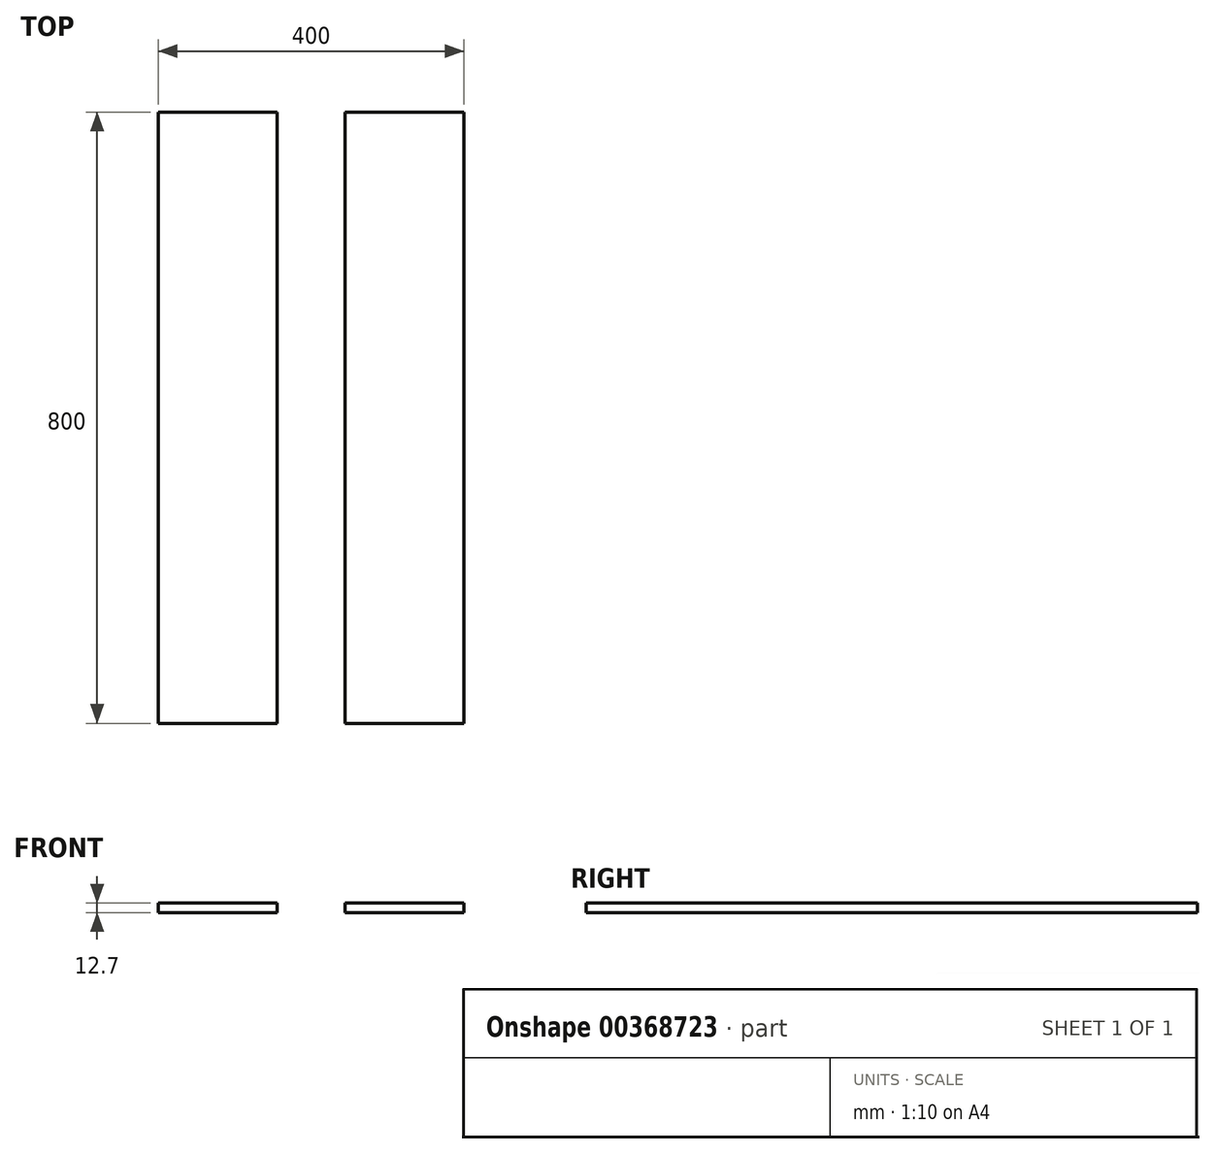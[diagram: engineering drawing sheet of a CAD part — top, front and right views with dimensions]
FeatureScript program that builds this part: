
annotation { "Feature Type Name" : "Feature", "Feature Type Description" : "" }
export const myFeature = defineFeature(function(context is Context, id is Id, definition is map)
    precondition{}
    {
        {
            var Q0;
            Q0=qCreatedBy(makeId("Top.planeOp"),FACE);
            var sketch = newSketch(context, id + "F0", { "sketchPlane" : qUnion([Q0])});
            skLineSegment(sketch, "E0.bottom", {"start": v(200, 400) * mm, "end": v(-200, 400) * mm});
            skLineSegment(sketch, "E0.top", {"start": v(200, -400) * mm, "end": v(-200, -400) * mm});
            skPoint(sketch, "E0.middle", {"position": v(0, 0) * mm});
            skLineSegment(sketch, "E1", {"start": v(-200, 400) * mm, "end": v(-200, -400) * mm});
            skLineSegment(sketch, "E2", {"start": v(200, 400) * mm, "end": v(200, -400) * mm});
            skLineSegment(sketch, "E3.bottom", {"start": v(44.45, 400) * mm, "end": v(-44.45, 400) * mm});
            skLineSegment(sketch, "E3.top", {"start": v(44.45, -400) * mm, "end": v(-44.45, -400) * mm});
            skLineSegment(sketch, "E3.left", {"start": v(44.45, 400) * mm, "end": v(44.45, -400) * mm});
            skLineSegment(sketch, "E3.right", {"start": v(-44.45, 400) * mm, "end": v(-44.45, -400) * mm});
            skSolve(sketch);
        }
        {
            var Q0;
            {var subQ0=sQuery(id+"F0.wireOp",EDGE,"E1");Q0=makeQuery(id+"F0.imprint","IMPRINT",FACE,{"disambiguationData":[TD([[makeQuery(id+"F0.imprint","IMPRINT",EDGE,{"derivedFrom":subQ0}),1.0]])]});}
            var Q1;
            Q1=makeQuery(id+"F0.imprint","IMPRINT",FACE,{"disambiguationData":[TD([[makeQuery(id+"F0.imprint","IMPRINT",EDGE,{"derivedFrom":sQuery(id+"F0.wireOp",EDGE,"E3.bottom")}),1.0]])]});
            var Q2;
            {var subQ0=sQuery(id+"F0.wireOp",EDGE,"E2");Q2=makeQuery(id+"F0.imprint","IMPRINT",FACE,{"disambiguationData":[TD([[makeQuery(id+"F0.imprint","IMPRINT",EDGE,{"derivedFrom":subQ0}),-1.0]])]});}
            extrude(context, id + "F1", {"entities" : qUnion([Q0, Q1, Q2]), "depth" : 12.7 * mm});
        }
    });
